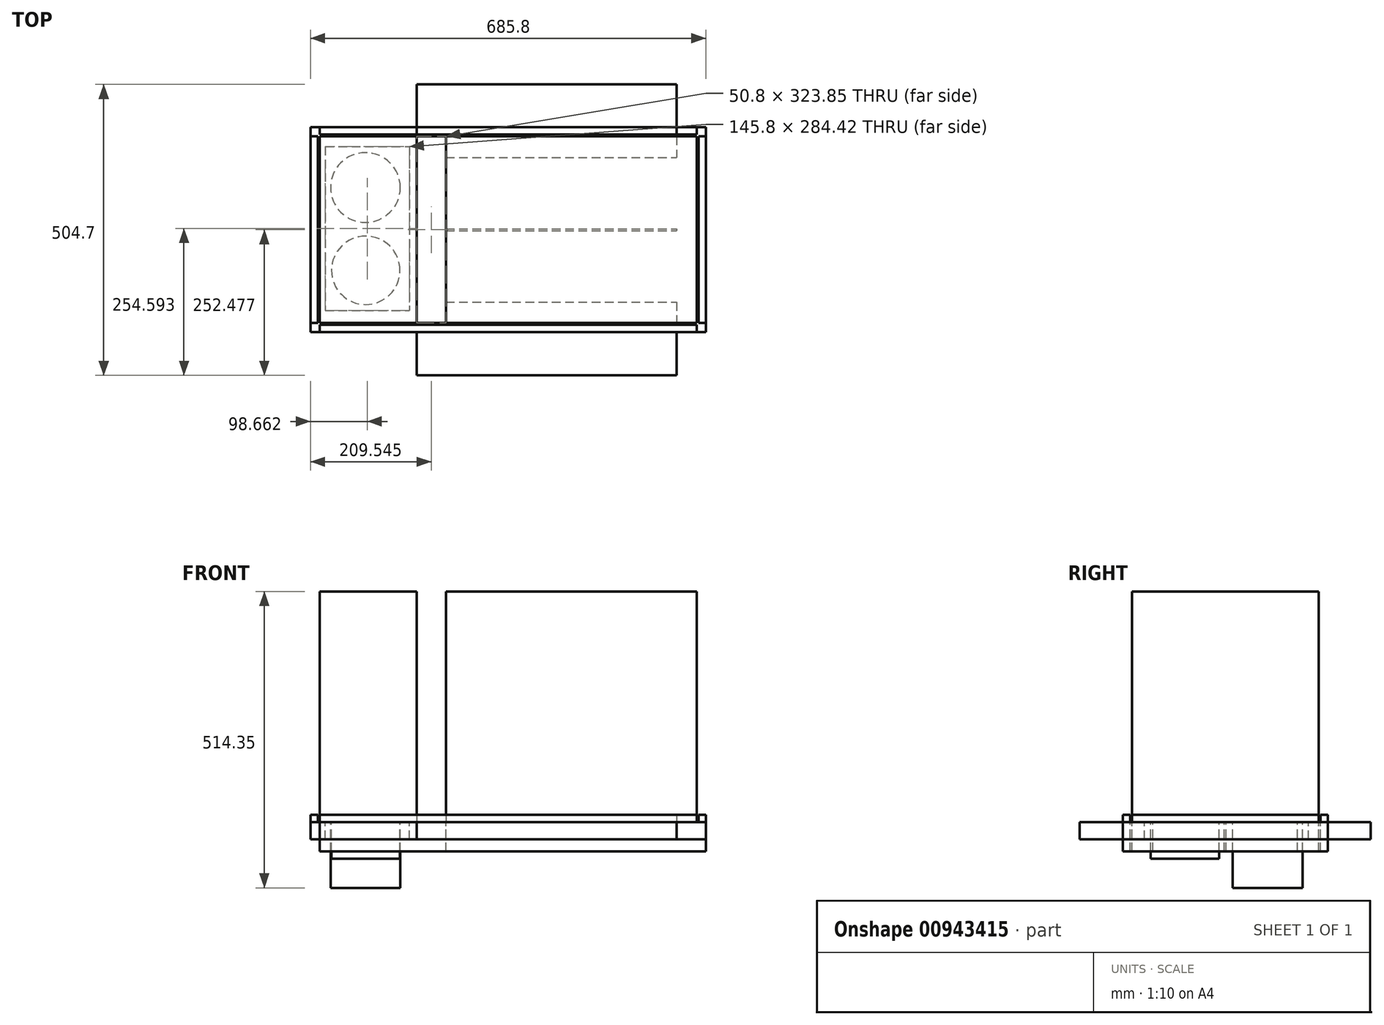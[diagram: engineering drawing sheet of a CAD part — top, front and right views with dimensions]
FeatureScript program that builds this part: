
annotation { "Feature Type Name" : "Feature", "Feature Type Description" : "" }
export const myFeature = defineFeature(function(context is Context, id is Id, definition is map)
    precondition{}
    {
        {
            var Q0;
            Q0=qCreatedBy(makeId("Top.planeOp"),FACE);
            var sketch = newSketch(context, id + "F0", { "sketchPlane" : qUnion([Q0])});
            skLineSegment(sketch, "E0.bottom", {"start": v(-366, 210.8) * mm, "end": v(288.04, 210.8) * mm});
            skLineSegment(sketch, "E0.top", {"start": v(-366, -113.05) * mm, "end": v(288.04, -113.05) * mm});
            skLineSegment(sketch, "E0.left", {"start": v(-366, 210.8) * mm, "end": v(-366, -113.05) * mm});
            skLineSegment(sketch, "E0.right", {"start": v(288.04, 210.8) * mm, "end": v(288.04, -113.05) * mm});
            skLineSegment(sketch, "E1.bottom", {"start": v(-381.88, 226.68) * mm, "end": v(303.92, 226.68) * mm});
            skLineSegment(sketch, "E1.top", {"start": v(-381.88, -128.92) * mm, "end": v(303.92, -128.92) * mm});
            skLineSegment(sketch, "E1.left", {"start": v(-381.88, 226.68) * mm, "end": v(-381.88, -128.92) * mm});
            skLineSegment(sketch, "E1.right", {"start": v(303.92, 226.68) * mm, "end": v(303.92, -128.92) * mm});
            skLineSegment(sketch, "E2.bottom", {"start": v(-197.73, 301.1) * mm, "end": v(303.92, 301.1) * mm});
            skLineSegment(sketch, "E2.top", {"start": v(-197.73, -203.6) * mm, "end": v(303.92, -203.6) * mm});
            skLineSegment(sketch, "E2.left", {"start": v(-197.73, 301.1) * mm, "end": v(-197.73, -203.6) * mm});
            skLineSegment(sketch, "E2.right", {"start": v(303.92, 301.1) * mm, "end": v(303.92, -203.6) * mm});
            skCircle(sketch, "E3", {"center": v(-285.99, -21.5) * mm, "radius": 59.35 * mm});
            skCircle(sketch, "E4", {"center": v(-286.51, 122.2) * mm, "radius": 60.48 * mm});
            skLineSegment(sketch, "E5.bottom", {"start": v(-356.12, 193.2) * mm, "end": v(-210.32, 193.2) * mm});
            skLineSegment(sketch, "E5.top", {"start": v(-356.12, -91.22) * mm, "end": v(-210.32, -91.22) * mm});
            skLineSegment(sketch, "E5.left", {"start": v(-356.12, 193.2) * mm, "end": v(-356.12, -91.22) * mm});
            skLineSegment(sketch, "E5.right", {"start": v(-210.32, 193.2) * mm, "end": v(-210.32, -91.22) * mm});
            skLineSegment(sketch, "E6.bottom", {"start": v(-381.88, 210.91) * mm, "end": v(-369.18, 210.91) * mm});
            skLineSegment(sketch, "E6.top", {"start": v(-381.88, -112.94) * mm, "end": v(-369.18, -112.94) * mm});
            skLineSegment(sketch, "E6.left", {"start": v(-381.88, 210.91) * mm, "end": v(-381.88, -112.94) * mm});
            skLineSegment(sketch, "E6.right", {"start": v(-369.18, 210.91) * mm, "end": v(-369.18, -112.94) * mm});
            skLineSegment(sketch, "E7.bottom", {"start": v(-366, -116.22) * mm, "end": v(288.04, -116.22) * mm});
            skLineSegment(sketch, "E7.top", {"start": v(-366, -128.92) * mm, "end": v(288.04, -128.92) * mm});
            skLineSegment(sketch, "E7.left", {"start": v(-366, -116.22) * mm, "end": v(-366, -128.92) * mm});
            skLineSegment(sketch, "E7.right", {"start": v(288.04, -116.22) * mm, "end": v(288.04, -128.92) * mm});
            skLineSegment(sketch, "E8.bottom", {"start": v(-366, 226.68) * mm, "end": v(288.04, 226.68) * mm});
            skLineSegment(sketch, "E8.top", {"start": v(-366, 213.98) * mm, "end": v(288.04, 213.98) * mm});
            skLineSegment(sketch, "E8.left", {"start": v(-366, 226.68) * mm, "end": v(-366, 213.98) * mm});
            skLineSegment(sketch, "E8.right", {"start": v(288.04, 226.68) * mm, "end": v(288.04, 213.98) * mm});
            skLineSegment(sketch, "E9.bottom", {"start": v(291.22, 210.8) * mm, "end": v(303.92, 210.8) * mm});
            skLineSegment(sketch, "E9.top", {"start": v(291.22, -113.05) * mm, "end": v(303.92, -113.05) * mm});
            skLineSegment(sketch, "E9.left", {"start": v(291.22, 210.8) * mm, "end": v(291.22, -113.05) * mm});
            skLineSegment(sketch, "E9.right", {"start": v(303.92, 210.8) * mm, "end": v(303.92, -113.05) * mm});
            skLineSegment(sketch, "E10.bottom", {"start": v(-197.73, -203.6) * mm, "end": v(-146.93, -203.6) * mm});
            skLineSegment(sketch, "E10.top", {"start": v(-197.73, 301.1) * mm, "end": v(-146.93, 301.1) * mm});
            skLineSegment(sketch, "E10.left", {"start": v(-197.73, -203.6) * mm, "end": v(-197.73, 301.1) * mm});
            skLineSegment(sketch, "E10.right", {"start": v(-146.93, -203.6) * mm, "end": v(-146.93, 301.1) * mm});
            skLineSegment(sketch, "E11.bottom", {"start": v(303.92, 301.1) * mm, "end": v(253.12, 301.1) * mm});
            skLineSegment(sketch, "E11.top", {"start": v(303.92, -203.6) * mm, "end": v(253.12, -203.6) * mm});
            skLineSegment(sketch, "E11.right", {"start": v(253.12, 301.1) * mm, "end": v(253.12, -203.6) * mm});
            skLineSegment(sketch, "E12.bottom", {"start": v(-146.93, -76.6) * mm, "end": v(253.12, -76.6) * mm});
            skLineSegment(sketch, "E12.top", {"start": v(-146.93, 50.4) * mm, "end": v(253.12, 50.4) * mm});
            skLineSegment(sketch, "E12.left", {"start": v(-146.93, -76.6) * mm, "end": v(-146.93, 50.4) * mm});
            skLineSegment(sketch, "E12.right", {"start": v(253.12, -76.6) * mm, "end": v(253.12, 50.4) * mm});
            skLineSegment(sketch, "E13.bottom", {"start": v(-146.93, 174.1) * mm, "end": v(253.12, 174.1) * mm});
            skLineSegment(sketch, "E13.top", {"start": v(-146.93, 47.1) * mm, "end": v(253.12, 47.1) * mm});
            skLineSegment(sketch, "E13.left", {"start": v(-146.93, 174.1) * mm, "end": v(-146.93, 47.1) * mm});
            skLineSegment(sketch, "E13.right", {"start": v(253.12, 174.1) * mm, "end": v(253.12, 47.1) * mm});
            skSolve(sketch);
        }
        {
            var Q0;
            {var subQ0=sQuery(id+"F0.wireOp",EDGE,"E0.left");Q0=makeQuery(id+"F0.imprint","IMPRINT",FACE,{"disambiguationData":[TD([[makeQuery(id+"F0.imprint","IMPRINT",EDGE,{"derivedFrom":subQ0}),1.0]])]});}
            var Q1;
            {var subQ0=sQuery(id+"F0.wireOp",EDGE,"E0.right");Q1=makeQuery(id+"F0.imprint","IMPRINT",FACE,{"disambiguationData":[TD([[makeQuery(id+"F0.imprint","IMPRINT",EDGE,{"derivedFrom":subQ0}),-1.0]])]});}
            var Q2;
            Q2=makeQuery(id+"F0.imprint","IMPRINT",FACE,{"disambiguationData":[TD([[makeQuery(id+"F0.imprint","IMPRINT",EDGE,{"derivedFrom":sQuery(id+"F0.wireOp",EDGE,"E3")}),-1.0]])]});
            var Q3;
            Q3=makeQuery(id+"F0.imprint","IMPRINT",FACE,{"disambiguationData":[TD([[makeQuery(id+"F0.imprint","IMPRINT",EDGE,{"derivedFrom":sQuery(id+"F0.wireOp",EDGE,"E4")}),1.0]])]});
            var Q4;
            Q4=makeQuery(id+"F0.imprint","IMPRINT",FACE,{"disambiguationData":[TD([[makeQuery(id+"F0.imprint","IMPRINT",EDGE,{"derivedFrom":sQuery(id+"F0.wireOp",EDGE,"E3")}),1.0]])]});
            var Q5;
            {var subQ0=sQuery(id+"F0.wireOp",EDGE,"E12.left");Q5=makeQuery(id+"F0.imprint","IMPRINT",FACE,{"disambiguationData":[TD([[makeQuery(id+"F0.imprint","IMPRINT",EDGE,{"derivedFrom":subQ0}),1.0]])]});}
            var Q6;
            Q6=makeQuery(id+"F0.imprint","IMPRINT",FACE,{"disambiguationData":[TD([[makeQuery(id+"F0.imprint","IMPRINT",EDGE,{"derivedFrom":sQuery(id+"F0.wireOp",EDGE,"E12.bottom")}),1.0]])]});
            var Q7;
            {var subQ5=sQuery(id+"F0.wireOp",EDGE,"E12.bottom");Q7=makeQuery(id+"F0.imprint","IMPRINT",FACE,{"disambiguationData":[TD([[makeQuery(id+"F0.imprint","IMPRINT",EDGE,{"derivedFrom":subQ5}),-1.0]])]});}
            var Q8;
            {var subQ5=sQuery(id+"F0.wireOp",EDGE,"E13.bottom");Q8=makeQuery(id+"F0.imprint","IMPRINT",FACE,{"disambiguationData":[TD([[makeQuery(id+"F0.imprint","IMPRINT",EDGE,{"derivedFrom":subQ5}),1.0]])]});}
            var Q9;
            {var subQ0=sQuery(id+"F0.wireOp",EDGE,"E12.top");Q9=makeQuery(id+"F0.imprint","IMPRINT",FACE,{"disambiguationData":[TD([[makeQuery(id+"F0.imprint","IMPRINT",EDGE,{"derivedFrom":subQ0}),1.0]])]});}
            var Q10;
            {var subQ0=sQuery(id+"F0.wireOp",EDGE,"E12.top");Q10=makeQuery(id+"F0.imprint","IMPRINT",FACE,{"disambiguationData":[TD([[makeQuery(id+"F0.imprint","IMPRINT",EDGE,{"derivedFrom":subQ0}),-1.0]])]});}
            extrude(context, id + "F1", {"entities" : qUnion([Q0, Q1, Q2, Q3, Q4, Q5, Q6, Q7, Q8, Q9, Q10]), "depth" : 400.05 * mm, "offsetDistance" : 25.4 * mm});
        }
        {
            var Q0;
            {var subQ5=sQuery(id+"F0.wireOp",EDGE,"E7.left");Q0=makeQuery(id+"F0.imprint","IMPRINT",FACE,{"disambiguationData":[TD([[makeQuery(id+"F0.imprint","IMPRINT",EDGE,{"derivedFrom":subQ5}),1.0]])]});}
            var Q1;
            {var subQ5=sQuery(id+"F0.wireOp",EDGE,"E7.right");Q1=makeQuery(id+"F0.imprint","IMPRINT",FACE,{"disambiguationData":[TD([[makeQuery(id+"F0.imprint","IMPRINT",EDGE,{"derivedFrom":subQ5}),-1.0]])]});}
            var Q2;
            Q2=makeQuery(id+"F0.imprint","IMPRINT",FACE,{"disambiguationData":[TD([[makeQuery(id+"F0.imprint","IMPRINT",EDGE,{"derivedFrom":sQuery(id+"F0.wireOp",EDGE,"E6.bottom")}),-1.0]])]});
            var Q3;
            {var subQ5=sQuery(id+"F0.wireOp",EDGE,"E8.left");Q3=makeQuery(id+"F0.imprint","IMPRINT",FACE,{"disambiguationData":[TD([[makeQuery(id+"F0.imprint","IMPRINT",EDGE,{"derivedFrom":subQ5}),1.0]])]});}
            var Q4;
            {var subQ5=sQuery(id+"F0.wireOp",EDGE,"E8.right");Q4=makeQuery(id+"F0.imprint","IMPRINT",FACE,{"disambiguationData":[TD([[makeQuery(id+"F0.imprint","IMPRINT",EDGE,{"derivedFrom":subQ5}),-1.0]])]});}
            var Q5;
            Q5=makeQuery(id+"F0.imprint","IMPRINT",FACE,{"disambiguationData":[TD([[makeQuery(id+"F0.imprint","IMPRINT",EDGE,{"derivedFrom":sQuery(id+"F0.wireOp",EDGE,"E9.bottom")}),-1.0]])]});
            var Q6;
            {var subQ0=sQuery(id+"F0.wireOp",EDGE,"E10.left");var subQ1=sQuery(id+"F0.wireOp",EDGE,"E8.bottom");var subQ2=makeQuery(id+"F0.imprint","INTERSECT",VERTEX,{"derivedFrom":[subQ1,subQ0]});Q6=makeQuery(id+"F0.imprint","IMPRINT",FACE,{"disambiguationData":[TD([[makeQuery(id+"F0.imprint","IMPRINT",EDGE,{"disambiguationData":[TD([[subQ2,-1.0]])],"derivedFrom":subQ1}),-1.0]])]});}
            var Q7;
            {var subQ0=sQuery(id+"F0.wireOp",EDGE,"E10.right");var subQ1=sQuery(id+"F0.wireOp",EDGE,"E8.bottom");var subQ2=makeQuery(id+"F0.imprint","INTERSECT",VERTEX,{"derivedFrom":[subQ1,subQ0]});Q7=makeQuery(id+"F0.imprint","IMPRINT",FACE,{"disambiguationData":[TD([[makeQuery(id+"F0.imprint","IMPRINT",EDGE,{"disambiguationData":[TD([[subQ2,-1.0]])],"derivedFrom":subQ1}),-1.0]])]});}
            var Q8;
            {var subQ0=sQuery(id+"F0.wireOp",EDGE,"E10.left");var subQ1=sQuery(id+"F0.wireOp",EDGE,"E7.bottom");var subQ2=makeQuery(id+"F0.imprint","INTERSECT",VERTEX,{"derivedFrom":[subQ1,subQ0]});Q8=makeQuery(id+"F0.imprint","IMPRINT",FACE,{"disambiguationData":[TD([[makeQuery(id+"F0.imprint","IMPRINT",EDGE,{"disambiguationData":[TD([[subQ2,-1.0]])],"derivedFrom":subQ1}),-1.0]])]});}
            var Q9;
            {var subQ0=sQuery(id+"F0.wireOp",EDGE,"E10.right");var subQ1=sQuery(id+"F0.wireOp",EDGE,"E7.bottom");var subQ2=makeQuery(id+"F0.imprint","INTERSECT",VERTEX,{"derivedFrom":[subQ1,subQ0]});Q9=makeQuery(id+"F0.imprint","IMPRINT",FACE,{"disambiguationData":[TD([[makeQuery(id+"F0.imprint","IMPRINT",EDGE,{"disambiguationData":[TD([[subQ2,-1.0]])],"derivedFrom":subQ1}),-1.0]])]});}
            extrude(context, id + "F2", {"entities" : qUnion([Q0, Q1, Q2, Q3, Q4, Q5, Q6, Q7, Q8, Q9]), "depth" : 12.7 * mm, "offsetDistance" : 25.4 * mm});
        }
        {
            var Q0;
            {var subQ0=sQuery(id+"F0.wireOp",EDGE,"E0.left");Q0=makeQuery(id+"F0.imprint","IMPRINT",FACE,{"disambiguationData":[TD([[makeQuery(id+"F0.imprint","IMPRINT",EDGE,{"derivedFrom":subQ0}),1.0]])]});}
            var Q1;
            {var subQ0=sQuery(id+"F0.wireOp",EDGE,"E0.right");Q1=makeQuery(id+"F0.imprint","IMPRINT",FACE,{"disambiguationData":[TD([[makeQuery(id+"F0.imprint","IMPRINT",EDGE,{"derivedFrom":subQ0}),-1.0]])]});}
            var Q2;
            {var subQ5=sQuery(id+"F0.wireOp",EDGE,"E7.left");Q2=makeQuery(id+"F0.imprint","IMPRINT",FACE,{"disambiguationData":[TD([[makeQuery(id+"F0.imprint","IMPRINT",EDGE,{"derivedFrom":subQ5}),1.0]])]});}
            var Q3;
            {var subQ5=sQuery(id+"F0.wireOp",EDGE,"E7.right");Q3=makeQuery(id+"F0.imprint","IMPRINT",FACE,{"disambiguationData":[TD([[makeQuery(id+"F0.imprint","IMPRINT",EDGE,{"derivedFrom":subQ5}),-1.0]])]});}
            var Q4;
            Q4=makeQuery(id+"F0.imprint","IMPRINT",FACE,{"disambiguationData":[TD([[makeQuery(id+"F0.imprint","IMPRINT",EDGE,{"derivedFrom":sQuery(id+"F0.wireOp",EDGE,"E6.bottom")}),-1.0]])]});
            var Q5;
            {var subQ5=sQuery(id+"F0.wireOp",EDGE,"E8.left");Q5=makeQuery(id+"F0.imprint","IMPRINT",FACE,{"disambiguationData":[TD([[makeQuery(id+"F0.imprint","IMPRINT",EDGE,{"derivedFrom":subQ5}),1.0]])]});}
            var Q6;
            {var subQ5=sQuery(id+"F0.wireOp",EDGE,"E8.right");Q6=makeQuery(id+"F0.imprint","IMPRINT",FACE,{"disambiguationData":[TD([[makeQuery(id+"F0.imprint","IMPRINT",EDGE,{"derivedFrom":subQ5}),-1.0]])]});}
            var Q7;
            Q7=makeQuery(id+"F0.imprint","IMPRINT",FACE,{"disambiguationData":[TD([[makeQuery(id+"F0.imprint","IMPRINT",EDGE,{"derivedFrom":sQuery(id+"F0.wireOp",EDGE,"E9.bottom")}),-1.0]])]});
            var Q8;
            {var subQ10=sQuery(id+"F0.wireOp",EDGE,"E0.right");Q8=makeQuery(id+"F0.imprint","IMPRINT",FACE,{"disambiguationData":[TD([[makeQuery(id+"F0.imprint","IMPRINT",EDGE,{"derivedFrom":subQ10}),1.0]])]});}
            var Q9;
            {var subQ0=sQuery(id+"F0.wireOp",EDGE,"E10.left");var subQ1=sQuery(id+"F0.wireOp",EDGE,"E7.bottom");var subQ2=makeQuery(id+"F0.imprint","INTERSECT",VERTEX,{"derivedFrom":[subQ1,subQ0]});Q9=makeQuery(id+"F0.imprint","IMPRINT",FACE,{"disambiguationData":[TD([[makeQuery(id+"F0.imprint","IMPRINT",EDGE,{"disambiguationData":[TD([[subQ2,-1.0]])],"derivedFrom":subQ1}),-1.0]])]});}
            var Q10;
            {var subQ0=sQuery(id+"F0.wireOp",EDGE,"E10.right");var subQ1=sQuery(id+"F0.wireOp",EDGE,"E7.bottom");var subQ2=makeQuery(id+"F0.imprint","INTERSECT",VERTEX,{"derivedFrom":[subQ1,subQ0]});Q10=makeQuery(id+"F0.imprint","IMPRINT",FACE,{"disambiguationData":[TD([[makeQuery(id+"F0.imprint","IMPRINT",EDGE,{"disambiguationData":[TD([[subQ2,-1.0]])],"derivedFrom":subQ1}),-1.0]])]});}
            var Q11;
            {var subQ0=sQuery(id+"F0.wireOp",EDGE,"E12.left");Q11=makeQuery(id+"F0.imprint","IMPRINT",FACE,{"disambiguationData":[TD([[makeQuery(id+"F0.imprint","IMPRINT",EDGE,{"derivedFrom":subQ0}),1.0]])]});}
            var Q12;
            {var subQ5=sQuery(id+"F0.wireOp",EDGE,"E12.bottom");Q12=makeQuery(id+"F0.imprint","IMPRINT",FACE,{"disambiguationData":[TD([[makeQuery(id+"F0.imprint","IMPRINT",EDGE,{"derivedFrom":subQ5}),-1.0]])]});}
            var Q13;
            Q13=makeQuery(id+"F0.imprint","IMPRINT",FACE,{"disambiguationData":[TD([[makeQuery(id+"F0.imprint","IMPRINT",EDGE,{"derivedFrom":sQuery(id+"F0.wireOp",EDGE,"E12.bottom")}),1.0]])]});
            var Q14;
            {var subQ0=sQuery(id+"F0.wireOp",EDGE,"E12.top");Q14=makeQuery(id+"F0.imprint","IMPRINT",FACE,{"disambiguationData":[TD([[makeQuery(id+"F0.imprint","IMPRINT",EDGE,{"derivedFrom":subQ0}),1.0]])]});}
            var Q15;
            {var subQ0=sQuery(id+"F0.wireOp",EDGE,"E10.left");var subQ1=sQuery(id+"F0.wireOp",EDGE,"E8.bottom");var subQ2=makeQuery(id+"F0.imprint","INTERSECT",VERTEX,{"derivedFrom":[subQ1,subQ0]});Q15=makeQuery(id+"F0.imprint","IMPRINT",FACE,{"disambiguationData":[TD([[makeQuery(id+"F0.imprint","IMPRINT",EDGE,{"disambiguationData":[TD([[subQ2,-1.0]])],"derivedFrom":subQ1}),-1.0]])]});}
            var Q16;
            {var subQ0=sQuery(id+"F0.wireOp",EDGE,"E10.right");var subQ1=sQuery(id+"F0.wireOp",EDGE,"E8.bottom");var subQ2=makeQuery(id+"F0.imprint","INTERSECT",VERTEX,{"derivedFrom":[subQ1,subQ0]});Q16=makeQuery(id+"F0.imprint","IMPRINT",FACE,{"disambiguationData":[TD([[makeQuery(id+"F0.imprint","IMPRINT",EDGE,{"disambiguationData":[TD([[subQ2,-1.0]])],"derivedFrom":subQ1}),-1.0]])]});}
            var Q17;
            {var subQ5=sQuery(id+"F0.wireOp",EDGE,"E13.bottom");Q17=makeQuery(id+"F0.imprint","IMPRINT",FACE,{"disambiguationData":[TD([[makeQuery(id+"F0.imprint","IMPRINT",EDGE,{"derivedFrom":subQ5}),1.0]])]});}
            var Q18;
            {var subQ0=sQuery(id+"F0.wireOp",EDGE,"E12.top");Q18=makeQuery(id+"F0.imprint","IMPRINT",FACE,{"disambiguationData":[TD([[makeQuery(id+"F0.imprint","IMPRINT",EDGE,{"derivedFrom":subQ0}),-1.0]])]});}
            var Q19;
            {var subQ0=sQuery(id+"F0.wireOp",EDGE,"E0.left");Q19=makeQuery(id+"F0.imprint","IMPRINT",FACE,{"disambiguationData":[TD([[makeQuery(id+"F0.imprint","IMPRINT",EDGE,{"derivedFrom":subQ0}),-1.0]])]});}
            var Q20;
            {var subQ0=sQuery(id+"F0.wireOp",EDGE,"E10.left");var subQ1=sQuery(id+"F0.wireOp",EDGE,"E0.bottom");var subQ2=makeQuery(id+"F0.imprint","INTERSECT",VERTEX,{"derivedFrom":[subQ1,subQ0]});Q20=makeQuery(id+"F0.imprint","IMPRINT",FACE,{"disambiguationData":[TD([[makeQuery(id+"F0.imprint","IMPRINT",EDGE,{"disambiguationData":[TD([[subQ2,-1.0]])],"derivedFrom":subQ1}),1.0]])]});}
            var Q21;
            {var subQ0=sQuery(id+"F0.wireOp",EDGE,"E10.right");var subQ1=sQuery(id+"F0.wireOp",EDGE,"E0.bottom");var subQ2=makeQuery(id+"F0.imprint","INTERSECT",VERTEX,{"derivedFrom":[subQ1,subQ0]});Q21=makeQuery(id+"F0.imprint","IMPRINT",FACE,{"disambiguationData":[TD([[makeQuery(id+"F0.imprint","IMPRINT",EDGE,{"disambiguationData":[TD([[subQ2,-1.0]])],"derivedFrom":subQ1}),1.0]])]});}
            var Q22;
            {var subQ0=sQuery(id+"F0.wireOp",EDGE,"E10.right");var subQ1=sQuery(id+"F0.wireOp",EDGE,"E0.top");var subQ2=makeQuery(id+"F0.imprint","INTERSECT",VERTEX,{"derivedFrom":[subQ1,subQ0]});Q22=makeQuery(id+"F0.imprint","IMPRINT",FACE,{"disambiguationData":[TD([[makeQuery(id+"F0.imprint","IMPRINT",EDGE,{"disambiguationData":[TD([[subQ2,-1.0]])],"derivedFrom":subQ1}),-1.0]])]});}
            var Q23;
            {var subQ0=sQuery(id+"F0.wireOp",EDGE,"E10.left");var subQ1=sQuery(id+"F0.wireOp",EDGE,"E0.top");var subQ2=makeQuery(id+"F0.imprint","INTERSECT",VERTEX,{"derivedFrom":[subQ1,subQ0]});Q23=makeQuery(id+"F0.imprint","IMPRINT",FACE,{"disambiguationData":[TD([[makeQuery(id+"F0.imprint","IMPRINT",EDGE,{"disambiguationData":[TD([[subQ2,-1.0]])],"derivedFrom":subQ1}),-1.0]])]});}
            var Q24;
            {var subQ5=sQuery(id+"F0.wireOp",EDGE,"E10.bottom");Q24=makeQuery(id+"F0.imprint","IMPRINT",FACE,{"disambiguationData":[TD([[makeQuery(id+"F0.imprint","IMPRINT",EDGE,{"derivedFrom":subQ5}),1.0]])]});}
            var Q25;
            {var subQ3=sQuery(id+"F0.wireOp",EDGE,"E11.top");Q25=makeQuery(id+"F0.imprint","IMPRINT",FACE,{"disambiguationData":[TD([[makeQuery(id+"F0.imprint","IMPRINT",EDGE,{"derivedFrom":subQ3}),-1.0]])]});}
            var Q26;
            {var subQ0=sQuery(id+"F0.wireOp",EDGE,"E2.top");Q26=makeQuery(id+"F0.imprint","IMPRINT",FACE,{"disambiguationData":[TD([[makeQuery(id+"F0.imprint","IMPRINT",EDGE,{"derivedFrom":subQ0}),1.0]])]});}
            var Q27;
            {var subQ5=sQuery(id+"F0.wireOp",EDGE,"E10.top");Q27=makeQuery(id+"F0.imprint","IMPRINT",FACE,{"disambiguationData":[TD([[makeQuery(id+"F0.imprint","IMPRINT",EDGE,{"derivedFrom":subQ5}),-1.0]])]});}
            var Q28;
            {var subQ0=sQuery(id+"F0.wireOp",EDGE,"E2.bottom");Q28=makeQuery(id+"F0.imprint","IMPRINT",FACE,{"disambiguationData":[TD([[makeQuery(id+"F0.imprint","IMPRINT",EDGE,{"derivedFrom":subQ0}),-1.0]])]});}
            var Q29;
            {var subQ3=sQuery(id+"F0.wireOp",EDGE,"E11.bottom");Q29=makeQuery(id+"F0.imprint","IMPRINT",FACE,{"disambiguationData":[TD([[makeQuery(id+"F0.imprint","IMPRINT",EDGE,{"derivedFrom":subQ3}),1.0]])]});}
            extrude(context, id + "F3", {"entities" : qUnion([Q0, Q1, Q2, Q3, Q4, Q5, Q6, Q7, Q8, Q9, Q10, Q11, Q12, Q13, Q14, Q15, Q16, Q17, Q18, Q19, Q20, Q21, Q22, Q23, Q24, Q25, Q26, Q27, Q28, Q29]), "depth" : 0 * mm, "offsetDistance" : 25.4 * mm, "hasSecondDirection" : true, "secondDirectionOppositeDirection" : true, "secondDirectionDepth" : 30.1 * mm});
        }
        {
            var Q0;
            {var subQ0=sQuery(id+"F0.wireOp",EDGE,"E12.left");Q0=makeQuery(id+"F0.imprint","IMPRINT",FACE,{"disambiguationData":[TD([[makeQuery(id+"F0.imprint","IMPRINT",EDGE,{"derivedFrom":subQ0}),1.0]])]});}
            var Q1;
            {var subQ5=sQuery(id+"F0.wireOp",EDGE,"E10.bottom");Q1=makeQuery(id+"F0.imprint","IMPRINT",FACE,{"disambiguationData":[TD([[makeQuery(id+"F0.imprint","IMPRINT",EDGE,{"derivedFrom":subQ5}),1.0]])]});}
            var Q2;
            {var subQ0=sQuery(id+"F0.wireOp",EDGE,"E10.left");var subQ1=sQuery(id+"F0.wireOp",EDGE,"E7.bottom");var subQ2=makeQuery(id+"F0.imprint","INTERSECT",VERTEX,{"derivedFrom":[subQ1,subQ0]});Q2=makeQuery(id+"F0.imprint","IMPRINT",FACE,{"disambiguationData":[TD([[makeQuery(id+"F0.imprint","IMPRINT",EDGE,{"disambiguationData":[TD([[subQ2,-1.0]])],"derivedFrom":subQ1}),-1.0]])]});}
            var Q3;
            {var subQ5=sQuery(id+"F0.wireOp",EDGE,"E10.top");Q3=makeQuery(id+"F0.imprint","IMPRINT",FACE,{"disambiguationData":[TD([[makeQuery(id+"F0.imprint","IMPRINT",EDGE,{"derivedFrom":subQ5}),-1.0]])]});}
            var Q4;
            {var subQ0=sQuery(id+"F0.wireOp",EDGE,"E10.left");var subQ1=sQuery(id+"F0.wireOp",EDGE,"E8.bottom");var subQ2=makeQuery(id+"F0.imprint","INTERSECT",VERTEX,{"derivedFrom":[subQ1,subQ0]});Q4=makeQuery(id+"F0.imprint","IMPRINT",FACE,{"disambiguationData":[TD([[makeQuery(id+"F0.imprint","IMPRINT",EDGE,{"disambiguationData":[TD([[subQ2,-1.0]])],"derivedFrom":subQ1}),-1.0]])]});}
            var Q5;
            Q5=makeQuery(id+"F0.imprint","IMPRINT",FACE,{"disambiguationData":[TD([[makeQuery(id+"F0.imprint","IMPRINT",EDGE,{"derivedFrom":sQuery(id+"F0.wireOp",EDGE,"E12.bottom")}),1.0]])]});
            var Q6;
            {var subQ0=sQuery(id+"F0.wireOp",EDGE,"E12.top");Q6=makeQuery(id+"F0.imprint","IMPRINT",FACE,{"disambiguationData":[TD([[makeQuery(id+"F0.imprint","IMPRINT",EDGE,{"derivedFrom":subQ0}),1.0]])]});}
            var Q7;
            {var subQ3=sQuery(id+"F0.wireOp",EDGE,"E11.top");Q7=makeQuery(id+"F0.imprint","IMPRINT",FACE,{"disambiguationData":[TD([[makeQuery(id+"F0.imprint","IMPRINT",EDGE,{"derivedFrom":subQ3}),-1.0]])]});}
            var Q8;
            {var subQ0=sQuery(id+"F0.wireOp",EDGE,"E0.right");Q8=makeQuery(id+"F0.imprint","IMPRINT",FACE,{"disambiguationData":[TD([[makeQuery(id+"F0.imprint","IMPRINT",EDGE,{"derivedFrom":subQ0}),-1.0]])]});}
            var Q9;
            {var subQ0=sQuery(id+"F0.wireOp",EDGE,"E7.right");Q9=makeQuery(id+"F0.imprint","IMPRINT",FACE,{"disambiguationData":[TD([[makeQuery(id+"F0.imprint","IMPRINT",EDGE,{"derivedFrom":subQ0}),-1.0]])]});}
            var Q10;
            {var subQ3=sQuery(id+"F0.wireOp",EDGE,"E11.bottom");Q10=makeQuery(id+"F0.imprint","IMPRINT",FACE,{"disambiguationData":[TD([[makeQuery(id+"F0.imprint","IMPRINT",EDGE,{"derivedFrom":subQ3}),1.0]])]});}
            var Q11;
            {var subQ0=sQuery(id+"F0.wireOp",EDGE,"E8.right");Q11=makeQuery(id+"F0.imprint","IMPRINT",FACE,{"disambiguationData":[TD([[makeQuery(id+"F0.imprint","IMPRINT",EDGE,{"derivedFrom":subQ0}),-1.0]])]});}
            var Q12;
            {var subQ11=sQuery(id+"F0.wireOp",EDGE,"E0.right");Q12=makeQuery(id+"F0.imprint","IMPRINT",FACE,{"disambiguationData":[TD([[makeQuery(id+"F0.imprint","IMPRINT",EDGE,{"derivedFrom":subQ11}),1.0]])]});}
            var Q13;
            {var subQ0=sQuery(id+"F0.wireOp",EDGE,"E10.left");var subQ1=sQuery(id+"F0.wireOp",EDGE,"E0.top");var subQ2=makeQuery(id+"F0.imprint","INTERSECT",VERTEX,{"derivedFrom":[subQ1,subQ0]});Q13=makeQuery(id+"F0.imprint","IMPRINT",FACE,{"disambiguationData":[TD([[makeQuery(id+"F0.imprint","IMPRINT",EDGE,{"disambiguationData":[TD([[subQ2,-1.0]])],"derivedFrom":subQ1}),-1.0]])]});}
            var Q14;
            {var subQ0=sQuery(id+"F0.wireOp",EDGE,"E10.left");var subQ1=sQuery(id+"F0.wireOp",EDGE,"E0.bottom");var subQ2=makeQuery(id+"F0.imprint","INTERSECT",VERTEX,{"derivedFrom":[subQ1,subQ0]});Q14=makeQuery(id+"F0.imprint","IMPRINT",FACE,{"disambiguationData":[TD([[makeQuery(id+"F0.imprint","IMPRINT",EDGE,{"disambiguationData":[TD([[subQ2,-1.0]])],"derivedFrom":subQ1}),1.0]])]});}
            var Q15;
            {var subQ0=sQuery(id+"F0.wireOp",EDGE,"E9.bottom");Q15=makeQuery(id+"F0.imprint","IMPRINT",FACE,{"disambiguationData":[TD([[makeQuery(id+"F0.imprint","IMPRINT",EDGE,{"derivedFrom":subQ0}),-1.0]])]});}
            extrude(context, id + "F4", {"entities" : qUnion([Q0, Q1, Q2, Q3, Q4, Q5, Q6, Q7, Q8, Q9, Q10, Q11, Q12, Q13, Q14, Q15]), "depth" : 0 * mm, "offsetDistance" : 25.4 * mm, "hasSecondDirection" : true, "secondDirectionOppositeDirection" : true, "secondDirectionDepth" : 50.8 * mm});
        }
        {
            var Q0;
            Q0=makeQuery(id+"F0.imprint","IMPRINT",FACE,{"disambiguationData":[TD([[makeQuery(id+"F0.imprint","IMPRINT",EDGE,{"derivedFrom":sQuery(id+"F0.wireOp",EDGE,"E4")}),1.0]])]});
            extrude(context, id + "F5", {"entities" : qUnion([Q0]), "operationType" : NewBodyOperationType.ADD, "depth" : 0 * mm, "offsetDistance" : 25.4 * mm, "hasSecondDirection" : true, "secondDirectionOppositeDirection" : true, "secondDirectionDepth" : 114.3 * mm});
        }
        {
            var Q0;
            Q0=makeQuery(id+"F0.imprint","IMPRINT",FACE,{"disambiguationData":[TD([[makeQuery(id+"F0.imprint","IMPRINT",EDGE,{"derivedFrom":sQuery(id+"F0.wireOp",EDGE,"E3")}),1.0]])]});
            extrude(context, id + "F6", {"entities" : qUnion([Q0]), "operationType" : NewBodyOperationType.ADD, "depth" : 0 * mm, "offsetDistance" : 25.4 * mm, "hasSecondDirection" : true, "secondDirectionOppositeDirection" : true, "secondDirectionDepth" : 63.5 * mm});
        }
        {
            var Q0;
            Q0=makeQuery(id+"F2.opExtrude","SWEPT_BODY",BODY,{"disambiguationData":[OSD([sQuery(id+"F0.wireOp",EDGE,"E8.bottom"),sQuery(id+"F0.wireOp",EDGE,"E8.top"),sQuery(id+"F0.wireOp",EDGE,"E8.left"),sQuery(id+"F0.wireOp",EDGE,"E8.right")])]});
            transform(context, id + "F7", {"entities" : qUnion([Q0]), "transformType" : TransformType.TRANSLATION_3D, "dx" : 0 * mm, "dy" : 0 * mm, "dz" : 0 * mm, "makeCopy" : true});
        }
    });
